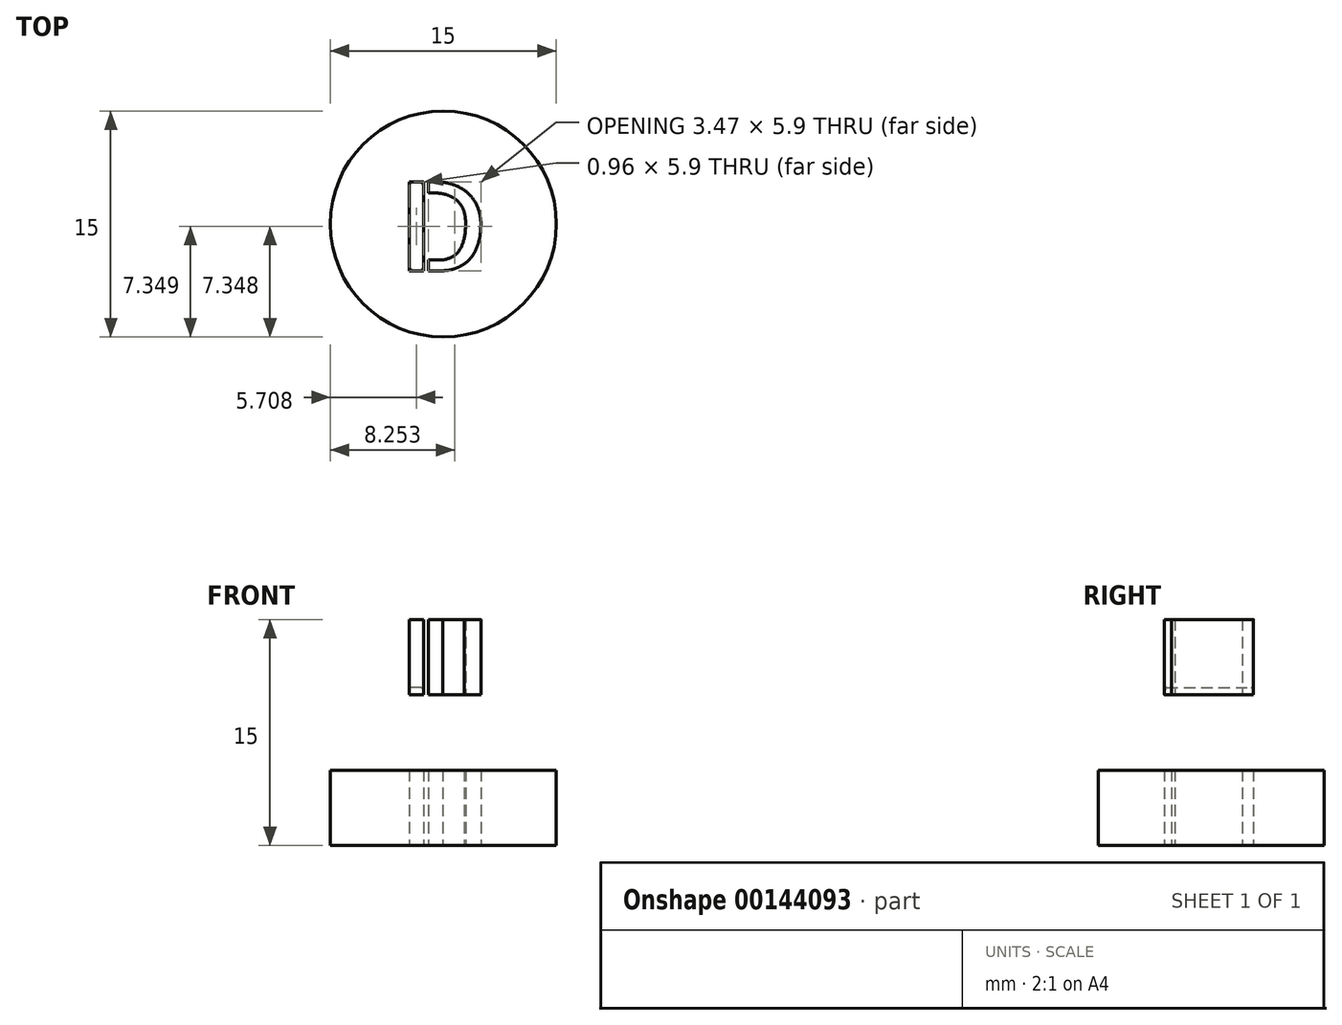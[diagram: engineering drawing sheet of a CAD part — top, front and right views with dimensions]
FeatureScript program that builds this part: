
annotation { "Feature Type Name" : "Feature", "Feature Type Description" : "" }
export const myFeature = defineFeature(function(context is Context, id is Id, definition is map)
    precondition{}
    {
        {
            var Q0;
            Q0=qCreatedBy(makeId("Top.planeOp"),FACE);
            var sketch = newSketch(context, id + "F4", { "sketchPlane" : qUnion([Q0])});
            skCircle(sketch, "E0", {"center": v(0, 0) * mm, "radius": 7.5 * mm});
            skText(sketch, "E1", { "text": "D", "fontName": "AllertaStencil-Regular.ttf"});
            const initialGuessFJiUFsX4Nzt5lbnQw_0  = {"E1": [-0.00304, -0.0031, 1, 0, 0.0059]};
            skSetInitialGuess(sketch, initialGuessFJiUFsX4Nzt5lbnQw_0);
            skSolve(sketch);
        }
        {
            var Q0;
            Q0=makeQuery(id+"F4.imprint","IMPRINT",FACE,{"disambiguationData":[TD([[makeQuery(id+"F4.imprint","IMPRINT",EDGE,{"derivedFrom":sQuery(id+"F4.wireOp",EDGE,"E0")}),1.0]])]});
            extrude(context, id + "F0", {"entities" : qUnion([Q0]), "depth" : 5 * mm});
        }
        {
            var Q0;
            Q0=makeQuery(id+"F4.imprint","IMPRINT",FACE,{"disambiguationData":[TD([[makeQuery(id+"F4.imprint","IMPRINT",EDGE,{"derivedFrom":sQuery(id+"F4.wireOp",EDGE,"E1.sketch_text.stroke-4")}),-1.0]])]});
            var Q1;
            Q1=makeQuery(id+"F4.imprint","IMPRINT",FACE,{"disambiguationData":[TD([[makeQuery(id+"F4.imprint","IMPRINT",EDGE,{"derivedFrom":sQuery(id+"F4.wireOp",EDGE,"E1.sketch_text.stroke-0")}),-1.0]])]});
            extrude(context, id + "F5", {"entities" : qUnion([Q0, Q1]), "operationType" : NewBodyOperationType.ADD, "depth" : 15 * mm});
        }
        {
            var Q0;
            Q0=makeQuery(id+"F4.imprint","IMPRINT",FACE,{"disambiguationData":[TD([[makeQuery(id+"F4.imprint","IMPRINT",EDGE,{"derivedFrom":sQuery(id+"F4.wireOp",EDGE,"E1.sketch_text.stroke-0")}),-1.0]])]});
            var Q1;
            Q1=makeQuery(id+"F4.imprint","IMPRINT",FACE,{"disambiguationData":[TD([[makeQuery(id+"F4.imprint","IMPRINT",EDGE,{"derivedFrom":sQuery(id+"F4.wireOp",EDGE,"E1.sketch_text.stroke-4")}),-1.0]])]});
            extrude(context, id + "F1", {"entities" : qUnion([Q0, Q1]), "operationType" : NewBodyOperationType.REMOVE, "depth" : 10 * mm});
        }
        {
            var Q0;
            Q0=makeQuery(id+"F1.boolean.opBoolean","COPY",FACE,{"derivedFrom":makeQuery(id+"F1.opExtrude","CAP_FACE",FACE,{"disambiguationData":[OSD([sQuery(id+"F4.wireOp",EDGE,"E1.sketch_text.stroke-0"),sQuery(id+"F4.wireOp",EDGE,"E1.sketch_text.stroke-1"),sQuery(id+"F4.wireOp",EDGE,"E1.sketch_text.stroke-2"),sQuery(id+"F4.wireOp",EDGE,"E1.sketch_text.stroke-3")])],"isStart":false})});
            extrude(context, id + "F2", {"entities" : qUnion([Q0]), "operationType" : NewBodyOperationType.REMOVE, "oppositeDirection" : true, "depth" : 0.5 * mm, "hasDraft" : true, "draftAngle" : 6 * degree, "draftPullDirection" : true});
        }
        {
            var Q0;
            Q0=makeQuery(id+"F2.boolean.opBoolean","COPY",FACE,{"derivedFrom":makeQuery(id+"F2.opExtrude","CAP_FACE",FACE,{"disambiguationData":[OSD([sQuery(id+"F4.wireOp",EDGE,"E1.sketch_text.stroke-0"),sQuery(id+"F4.wireOp",EDGE,"E1.sketch_text.stroke-1"),sQuery(id+"F4.wireOp",EDGE,"E1.sketch_text.stroke-2"),sQuery(id+"F4.wireOp",EDGE,"E1.sketch_text.stroke-3")])],"isStart":false})});
            fillet(context, id + "F3", {"entities" : qUnion([Q0]), "radius" : 0.1 * mm, "tangentPropagation" : true, "allowEdgeOverflow" : false});
        }
    });
